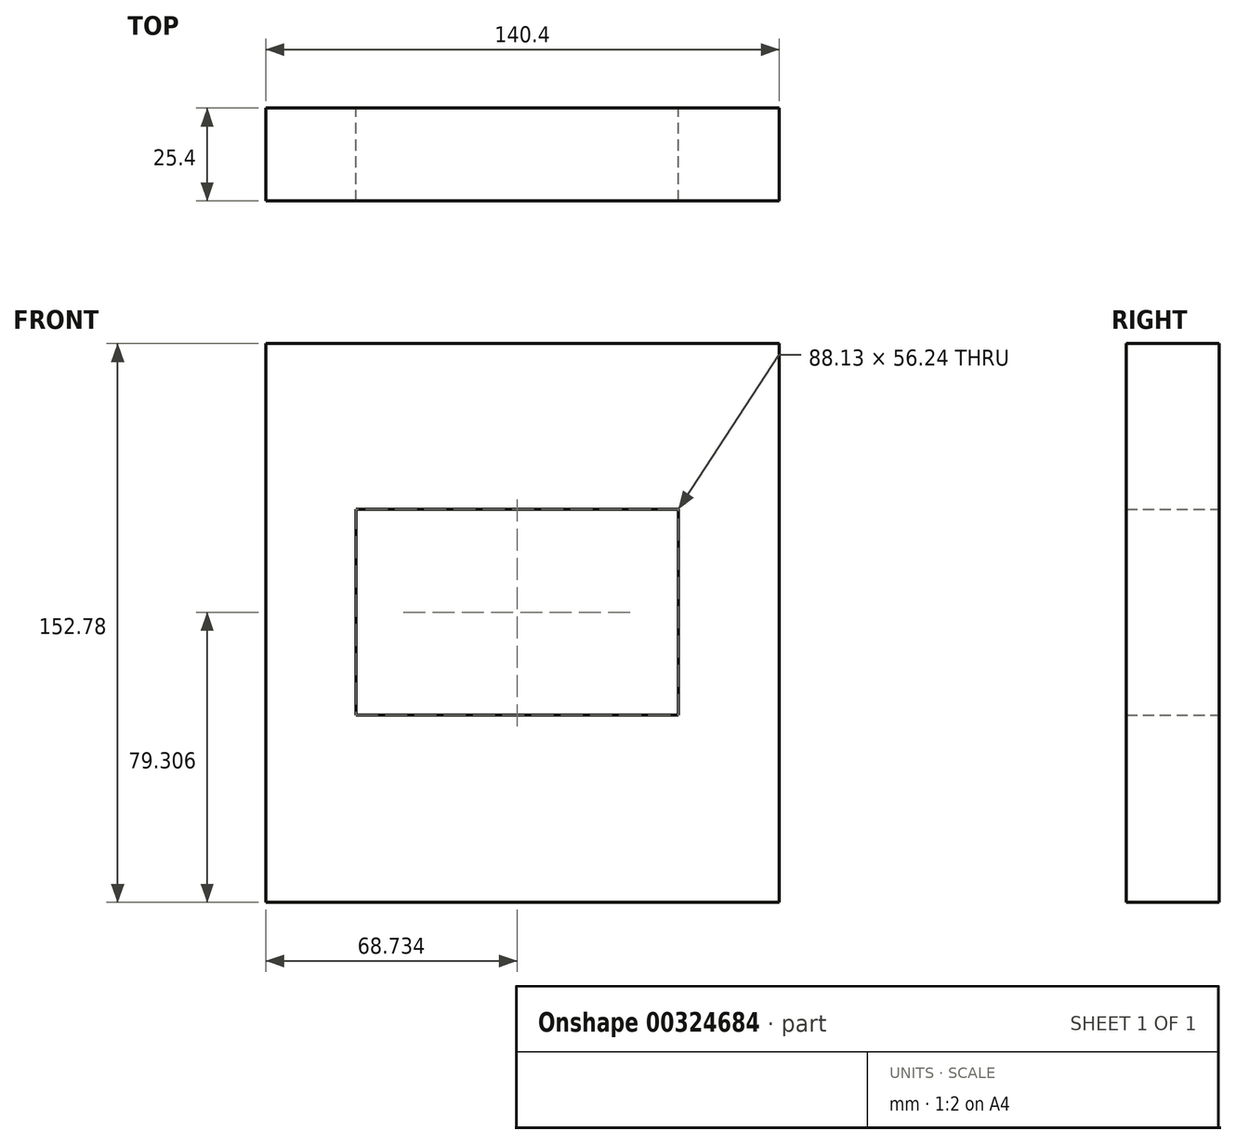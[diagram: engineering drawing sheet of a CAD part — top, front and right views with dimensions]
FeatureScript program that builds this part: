
annotation { "Feature Type Name" : "Feature", "Feature Type Description" : "" }
export const myFeature = defineFeature(function(context is Context, id is Id, definition is map)
    precondition{}
    {
        {
            var Q0;
            Q0=qCreatedBy(makeId("Front.planeOp"),FACE);
            var sketch = newSketch(context, id + "F0", { "sketchPlane" : qUnion([Q0])});
            skLineSegment(sketch, "E0.bottom", {"start": v(-69.56, 79.35) * mm, "end": v(70.84, 79.35) * mm});
            skLineSegment(sketch, "E0.top", {"start": v(-69.56, -73.43) * mm, "end": v(70.84, -73.43) * mm});
            skLineSegment(sketch, "E0.left", {"start": v(-69.56, 79.35) * mm, "end": v(-69.56, -73.43) * mm});
            skLineSegment(sketch, "E0.right", {"start": v(70.84, 79.35) * mm, "end": v(70.84, -73.43) * mm});
            skLineSegment(sketch, "E1.bottom", {"start": v(43.24, 34) * mm, "end": v(-44.89, 34) * mm});
            skLineSegment(sketch, "E1.top", {"start": v(43.24, -22.25) * mm, "end": v(-44.89, -22.25) * mm});
            skLineSegment(sketch, "E1.left", {"start": v(43.24, 34) * mm, "end": v(43.24, -22.25) * mm});
            skLineSegment(sketch, "E1.right", {"start": v(-44.89, 34) * mm, "end": v(-44.89, -22.25) * mm});
            skSolve(sketch);
        }
        {
            var Q0;
            Q0 = qSketchRegion(id + "F0", true);
            extrude(context, id + "F1", {"entities" : qUnion([Q0]), "depth" : 25.4 * mm});
        }
    });
